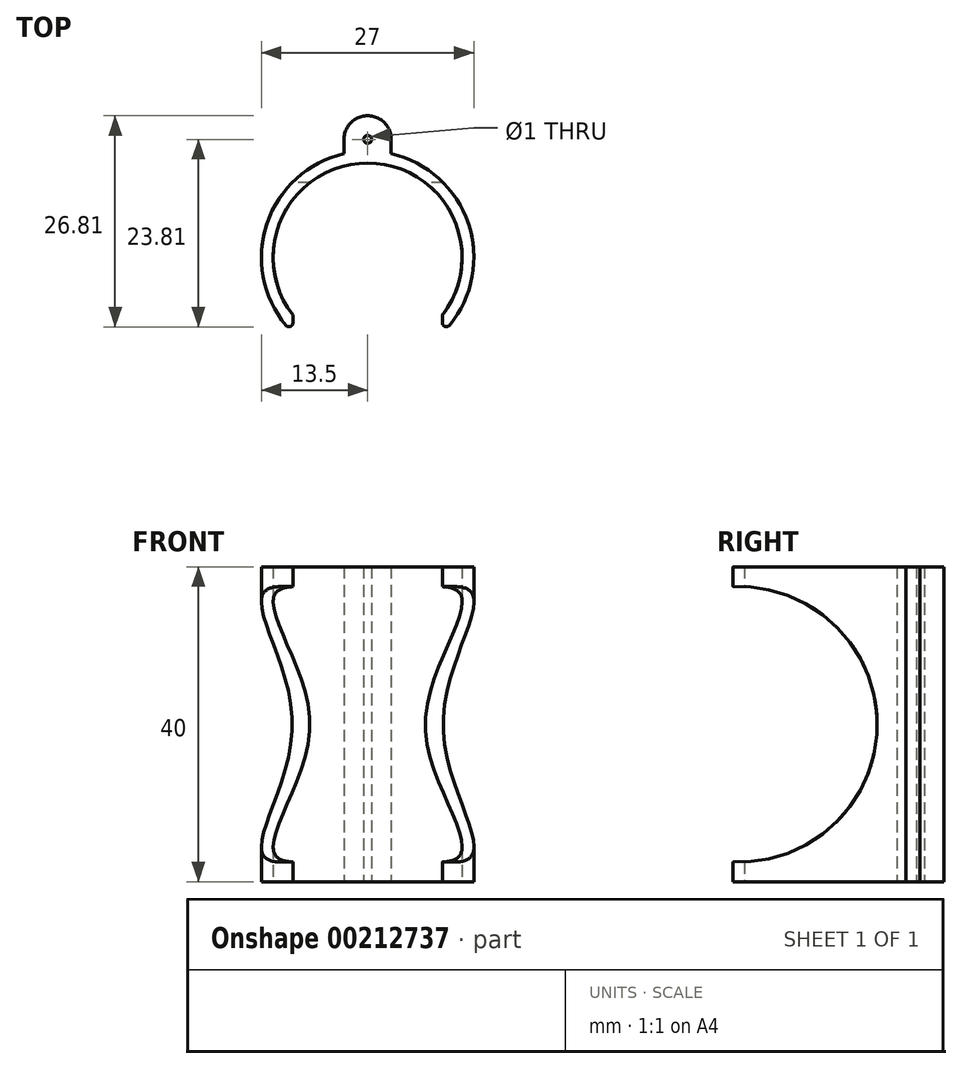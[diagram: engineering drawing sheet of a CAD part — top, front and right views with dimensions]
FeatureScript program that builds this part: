
annotation { "Feature Type Name" : "Feature", "Feature Type Description" : "" }
export const myFeature = defineFeature(function(context is Context, id is Id, definition is map)
    precondition{}
    {
        {
            var Q0;
            Q0=qCreatedBy(makeId("Top.planeOp"),FACE);
            var sketch = newSketch(context, id + "F0", { "sketchPlane" : qUnion([Q0])});
            skArc(sketch, "E0", {"start": v(9.5, -7.33) * mm, "mid": v(0, 12) * mm, "end": v(-9.5, -7.33) * mm});
            skArc(sketch, "E1", {"start": v(9.5, -9.6) * mm, "mid": v(0, 13.5) * mm, "end": v(-9.5, -9.6) * mm});
            skLineSegment(sketch, "E2", {"start": v(-9.5, -7.33) * mm, "end": v(-9.5, -9.6) * mm});
            skLineSegment(sketch, "E3.MirrorCS", {"start": v(9.5, -7.33) * mm, "end": v(9.5, -9.6) * mm});
            skSolve(sketch);
        }
        {
            var Q0;
            Q0 = qSketchRegion(id + "F0", true);
            extrude(context, id + "F1", {"entities" : qUnion([Q0]), "depth" : 40 * mm});
        }
        {
            var Q0;
            Q0=qCreatedBy(makeId("Right.planeOp"),FACE);
            var sketch = newSketch(context, id + "F2", { "sketchPlane" : qUnion([Q0])});
            skCircle(sketch, "E4", {"center": v(-8, 20) * mm, "radius": 17.5 * mm});
            skSolve(sketch);
        }
        {
            var Q0;
            Q0=makeQuery(id+"F2.imprint","IMPRINT",FACE,{"disambiguationData":[TD([[makeQuery(id+"F2.imprint","IMPRINT",EDGE,{"derivedFrom":sQuery(id+"F2.wireOp",EDGE,"E4")}),1.0]])]});
            extrude(context, id + "F3", {"entities" : qUnion([Q0]), "endBound" : BoundingType.SYMMETRIC, "depth" : 30 * mm});
        }
        {
            var Q0;
            Q0=makeQuery(id+"F3.opExtrude","SWEPT_BODY",BODY,{"disambiguationData":[OSD([sQuery(id+"F2.wireOp",EDGE,"E4")])]});
            var Q1;
            Q1=makeQuery(id+"F1.opExtrude","SWEPT_BODY",BODY,{"disambiguationData":[OSD([sQuery(id+"F0.wireOp",EDGE,"E0"),sQuery(id+"F0.wireOp",EDGE,"E1"),sQuery(id+"F0.wireOp",EDGE,"E2"),sQuery(id+"F0.wireOp",EDGE,"E3.MirrorCS")])]});
            booleanBodies(context, id + "F4", {"operationType" : BooleanOperationType.SUBTRACTION, "tools" : qUnion([Q0]), "targets" : qUnion([Q1])});
        }
        {
            var Q0;
            Q0=qCreatedBy(makeId("Top.planeOp"),FACE);
            var sketch = newSketch(context, id + "F5", { "sketchPlane" : qUnion([Q0])});
            skArc(sketch, "E5", {"start": v(3, 14.96) * mm, "mid": v(0, 18) * mm, "end": v(-3, 14.96) * mm});
            skArc(sketch, "E6.0", {"start": v(3, 13.16) * mm, "mid": v(0, 13.5) * mm, "end": v(-3, 13.16) * mm});
            skLineSegment(sketch, "E7", {"start": v(3, 14.96) * mm, "end": v(3, 13.16) * mm});
            skLineSegment(sketch, "E8.MirrorCS", {"start": v(-3, 14.96) * mm, "end": v(-3, 13.16) * mm});
            skPoint(sketch, "E9.orphan", {"position": v(-9.5, -9.6) * mm});
            skPoint(sketch, "E10.orphan", {"position": v(9.5, -9.6) * mm});
            skCircle(sketch, "E11", {"center": v(0, 15) * mm, "radius": 0.5 * mm});
            skSolve(sketch);
        }
        {
            var Q0;
            Q0=makeQuery(id+"F5.imprint","IMPRINT",FACE,{"disambiguationData":[TD([[makeQuery(id+"F5.imprint","IMPRINT",EDGE,{"derivedFrom":sQuery(id+"F5.wireOp",EDGE,"E5")}),1.0]])]});
            extrude(context, id + "F6", {"entities" : qUnion([Q0]), "operationType" : NewBodyOperationType.ADD, "depth" : 40 * mm});
        }
        {
            var Q0;
            {var subQ0=sQuery(id+"F0.wireOp",EDGE,"E2");var subQ1=sQuery(id+"F0.wireOp",EDGE,"E1");Q0=makeQuery(id+"F4.opBoolean","SPLIT",EDGE,{"disambiguationData":[TD([makeQuery(id+"F1.opExtrude","CAP_FACE",FACE,{"disambiguationData":[OSD([sQuery(id+"F0.wireOp",EDGE,"E0"),subQ1,subQ0,sQuery(id+"F0.wireOp",EDGE,"E3.MirrorCS")])],"isStart":false})])],"derivedFrom":makeQuery(id+"F1.opExtrude","SWEPT_EDGE",EDGE,{"disambiguationData":[OSD([subQ1,subQ0])]})});}
            var Q1;
            {var subQ0=sQuery(id+"F0.wireOp",EDGE,"E3.MirrorCS");var subQ1=sQuery(id+"F0.wireOp",EDGE,"E1");Q1=makeQuery(id+"F4.opBoolean","SPLIT",EDGE,{"disambiguationData":[TD([makeQuery(id+"F1.opExtrude","CAP_FACE",FACE,{"disambiguationData":[OSD([sQuery(id+"F0.wireOp",EDGE,"E0"),subQ1,sQuery(id+"F0.wireOp",EDGE,"E2"),subQ0])],"isStart":false})])],"derivedFrom":makeQuery(id+"F1.opExtrude","SWEPT_EDGE",EDGE,{"disambiguationData":[OSD([subQ1,subQ0])]})});}
            var Q2;
            {var subQ0=sQuery(id+"F0.wireOp",EDGE,"E3.MirrorCS");var subQ1=sQuery(id+"F0.wireOp",EDGE,"E1");Q2=makeQuery(id+"F4.opBoolean","SPLIT",EDGE,{"disambiguationData":[TD([makeQuery(id+"F1.opExtrude","CAP_FACE",FACE,{"disambiguationData":[OSD([sQuery(id+"F0.wireOp",EDGE,"E0"),subQ1,sQuery(id+"F0.wireOp",EDGE,"E2"),subQ0])],"isStart":true})])],"derivedFrom":makeQuery(id+"F1.opExtrude","SWEPT_EDGE",EDGE,{"disambiguationData":[OSD([subQ1,subQ0])]})});}
            var Q3;
            {var subQ0=sQuery(id+"F0.wireOp",EDGE,"E2");var subQ1=sQuery(id+"F0.wireOp",EDGE,"E1");Q3=makeQuery(id+"F4.opBoolean","SPLIT",EDGE,{"disambiguationData":[TD([makeQuery(id+"F1.opExtrude","CAP_FACE",FACE,{"disambiguationData":[OSD([sQuery(id+"F0.wireOp",EDGE,"E0"),subQ1,subQ0,sQuery(id+"F0.wireOp",EDGE,"E3.MirrorCS")])],"isStart":true})])],"derivedFrom":makeQuery(id+"F1.opExtrude","SWEPT_EDGE",EDGE,{"disambiguationData":[OSD([subQ1,subQ0])]})});}
            fillet(context, id + "F7", {"entities" : qUnion([Q0, Q1, Q2, Q3]), "radius" : .5 * mm, "tangentPropagation" : true, "allowEdgeOverflow" : false});
        }
    });
